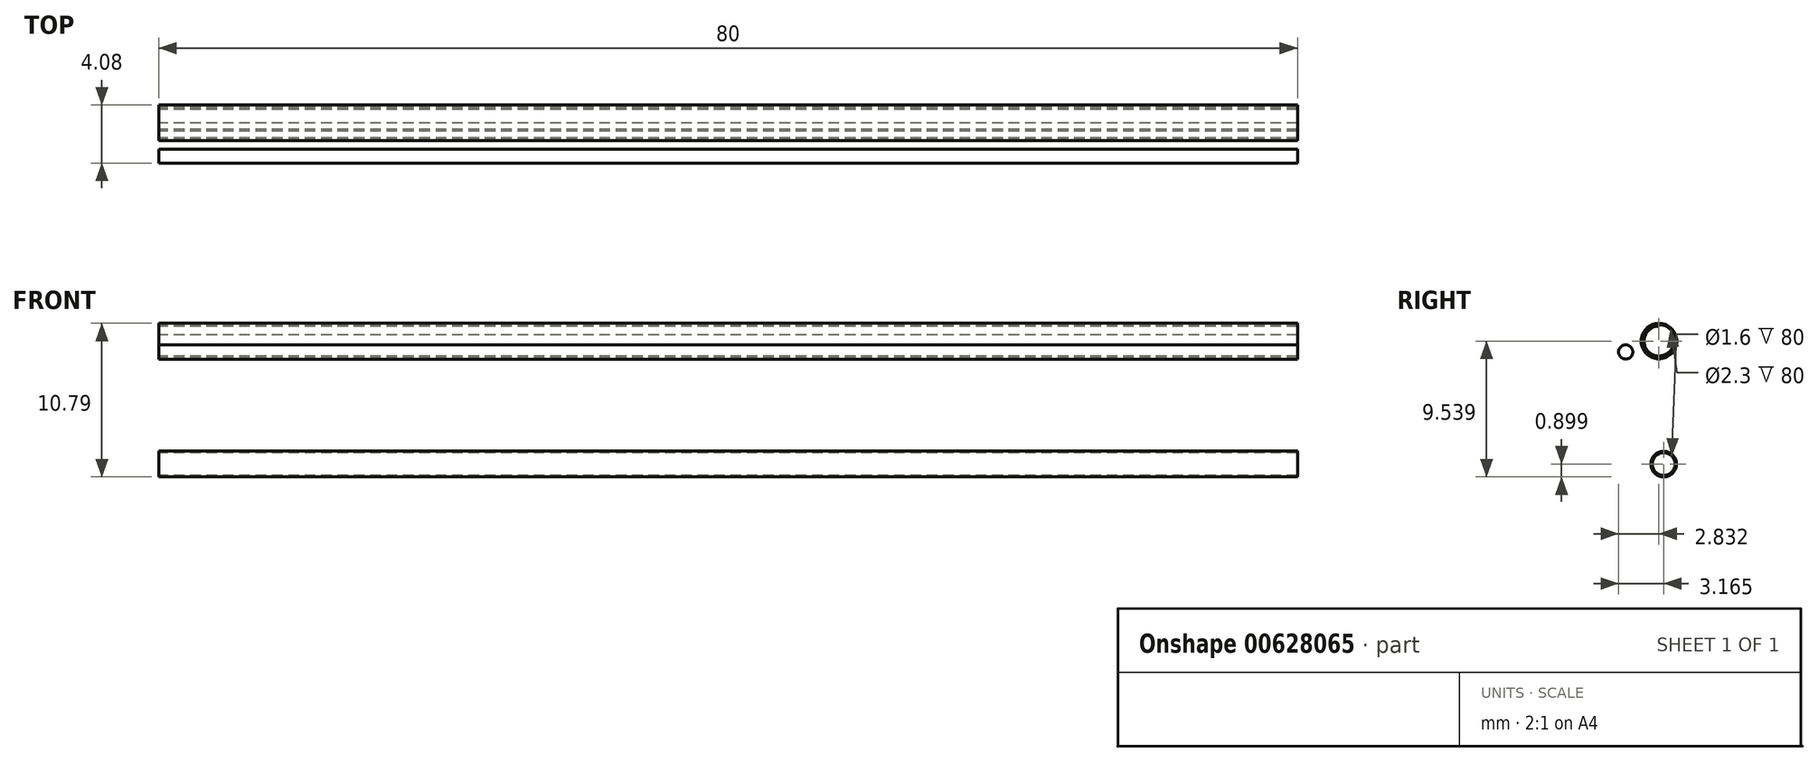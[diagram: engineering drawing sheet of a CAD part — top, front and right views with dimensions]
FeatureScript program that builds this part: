
annotation { "Feature Type Name" : "Feature", "Feature Type Description" : "" }
export const myFeature = defineFeature(function(context is Context, id is Id, definition is map)
    precondition{}
    {
        {
            var Q0;
            Q0=qCreatedBy(makeId("Right.planeOp"),FACE);
            var sketch = newSketch(context, id + "F0", { "sketchPlane" : qUnion([Q0])});
            skCircle(sketch, "E0", {"center": v(15.9, 33.76) * mm, "radius": 1.25 * mm});
            skCircle(sketch, "E1.0", {"center": v(15.9, 33.76) * mm, "radius": 1.15 * mm});
            skSolve(sketch);
        }
        {
            var Q0;
            Q0 = qSketchRegion(id + "F0", true);
            extrude(context, id + "F1", {"entities" : qUnion([Q0]), "depth" : 80 * mm, "offsetDistance" : 25 * mm});
        }
        {
            var Q0;
            Q0=qCreatedBy(makeId("Right.planeOp"),FACE);
            var sketch = newSketch(context, id + "F2", { "sketchPlane" : qUnion([Q0])});
            skCircle(sketch, "E2", {"center": v(16.22, 25.12) * mm, "radius": 0.9 * mm});
            skCircle(sketch, "E3.0", {"center": v(16.22, 25.12) * mm, "radius": 0.8 * mm});
            skSolve(sketch);
        }
        {
            var Q0;
            Q0 = qSketchRegion(id + "F2", true);
            extrude(context, id + "F3", {"entities" : qUnion([Q0]), "depth" : 80 * mm, "offsetDistance" : 25 * mm});
        }
        {
            var Q0;
            Q0=qCreatedBy(makeId("Right.planeOp"),FACE);
            var sketch = newSketch(context, id + "F4", { "sketchPlane" : qUnion([Q0])});
            skArc(sketch, "E4", {"start": v(15.9, 34.86) * mm, "mid": v(15.3, 32.84) * mm, "end": v(16.9, 34.2) * mm});
            skLineSegment(sketch, "E5", {"start": v(15.9, 33.76) * mm, "end": v(15.9, 32.66) * mm});
            skArc(sketch, "E6.0", {"start": v(15.9, 34.81) * mm, "mid": v(15.32, 32.88) * mm, "end": v(16.85, 34.19) * mm});
            skLineSegment(sketch, "E7", {"start": v(15.9, 34.86) * mm, "end": v(15.9, 34.81) * mm});
            skLineSegment(sketch, "E8", {"start": v(16.9, 34.2) * mm, "end": v(16.85, 34.19) * mm});
            skSolve(sketch);
        }
        {
            var Q0;
            {var subQ0=sQuery(id+"F4.wireOp",EDGE,"E7");Q0=makeQuery(id+"F4.imprint","IMPRINT",FACE,{"disambiguationData":[TD([[makeQuery(id+"F4.imprint","IMPRINT",EDGE,{"derivedFrom":subQ0}),-1.0]])]});}
            var Q1;
            {var subQ0=sQuery(id+"F4.wireOp",EDGE,"E8");Q1=makeQuery(id+"F4.imprint","IMPRINT",FACE,{"disambiguationData":[TD([[makeQuery(id+"F4.imprint","IMPRINT",EDGE,{"derivedFrom":subQ0}),1.0]])]});}
            extrude(context, id + "F5", {"entities" : qUnion([Q0, Q1]), "depth" : 80 * mm, "offsetDistance" : 25 * mm});
        }
        {
            var Q0;
            Q0=qCreatedBy(makeId("Right.planeOp"),FACE);
            var sketch = newSketch(context, id + "F6", { "sketchPlane" : qUnion([Q0])});
            skCircle(sketch, "E9", {"center": v(13.56, 33) * mm, "radius": 0.5 * mm});
            skSolve(sketch);
        }
        {
            var Q0;
            Q0 = qSketchRegion(id + "F6", true);
            extrude(context, id + "F7", {"entities" : qUnion([Q0]), "depth" : 80 * mm, "offsetDistance" : 25 * mm});
        }
    });
